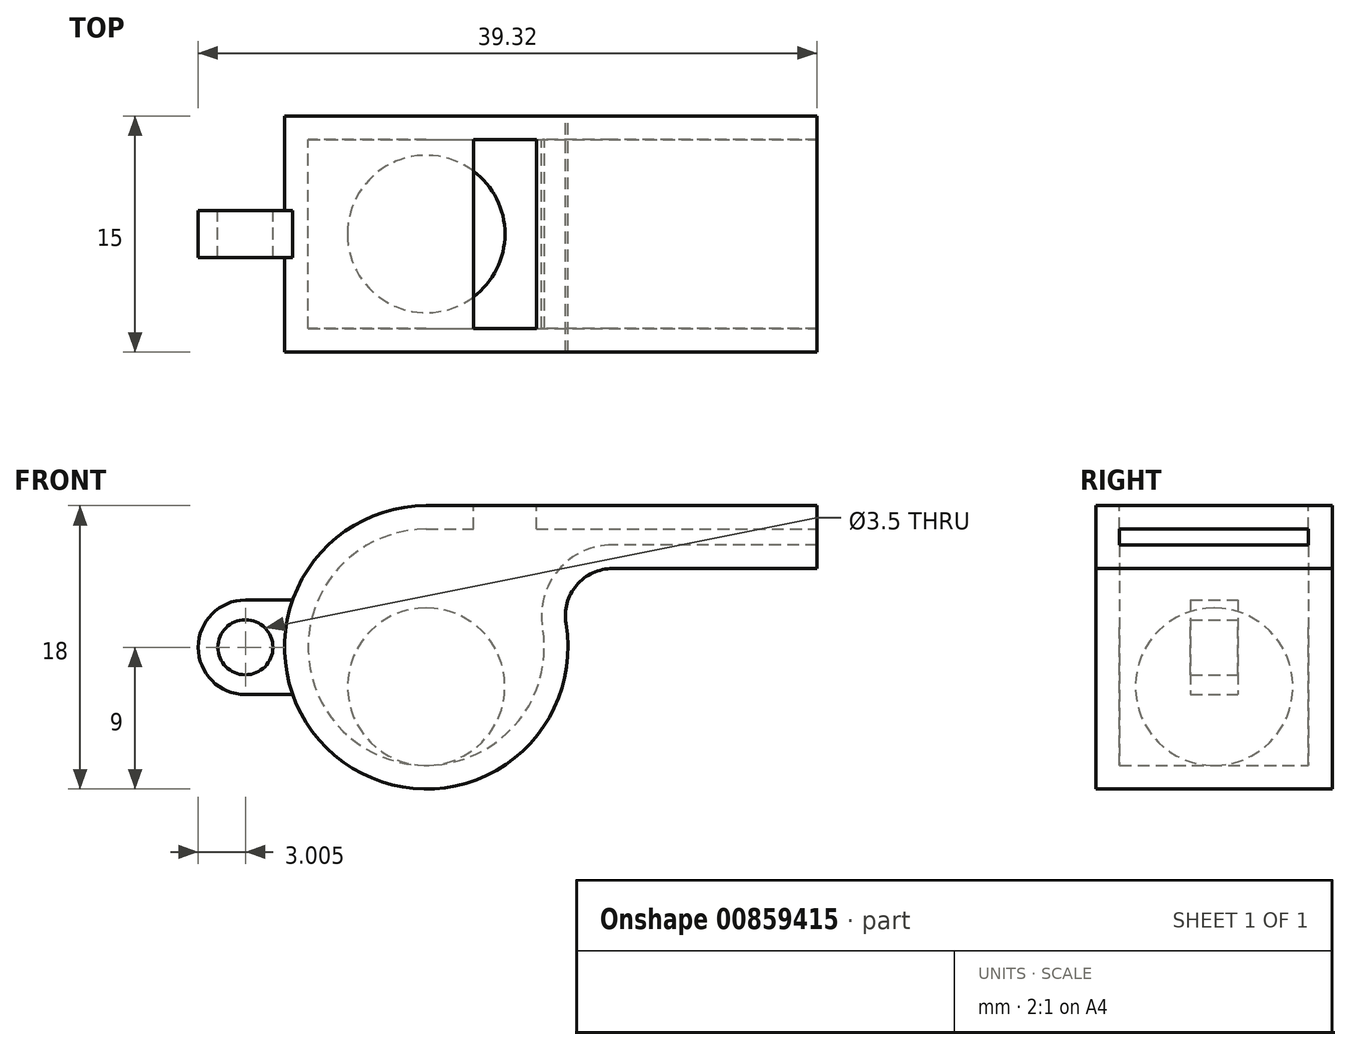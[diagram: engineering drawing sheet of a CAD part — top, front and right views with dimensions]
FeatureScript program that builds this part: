
annotation { "Feature Type Name" : "Feature", "Feature Type Description" : "" }
export const myFeature = defineFeature(function(context is Context, id is Id, definition is map)
    precondition{}
    {
        {
            var Q0;
            Q0=qCreatedBy(makeId("Front.planeOp"),FACE);
            var sketch = newSketch(context, id + "F0", { "sketchPlane" : qUnion([Q0])});
            skArc(sketch, "E0", {"start": v(0, 9) * mm, "mid": v(-5.8, -6.87) * mm, "end": v(8.87, 1.5) * mm});
            skLineSegment(sketch, "E1", {"start": v(0, 9) * mm, "end": v(24.83, 9) * mm});
            skLineSegment(sketch, "E2", {"start": v(24.83, 5) * mm, "end": v(11.83, 5) * mm});
            skArc(sketch, "E3.filletArc", {"start": v(11.83, 5) * mm, "mid": v(9.54, 3.94) * mm, "end": v(8.87, 1.5) * mm});
            skLineSegment(sketch, "E4", {"start": v(24.83, 9) * mm, "end": v(24.83, 5) * mm});
            skSolve(sketch);
        }
        {
            var Q0;
            Q0=makeQuery(id+"F0.imprint","IMPRINT",FACE,{"disambiguationData":[TD([[makeQuery(id+"F0.imprint","IMPRINT",EDGE,{"derivedFrom":sQuery(id+"F0.wireOp",EDGE,"E0")}),1.0]])]});
            extrude(context, id + "F1", {"entities" : qUnion([Q0]), "endBound" : BoundingType.SYMMETRIC, "depth" : 15 * mm, "offsetDistance" : 25 * mm});
        }
        {
            var Q0;
            Q0=makeQuery(id+"F1.opExtrude","SWEPT_FACE",FACE,{"disambiguationData":[OSD([sQuery(id+"F0.wireOp",EDGE,"E4")])]});
            shell(context, id + "F2", {"entities" : qUnion([Q0]), "thickness" : 1.5 * mm});
        }
        {
            var Q0;
            Q0=makeQuery(id+"F1.opExtrude","SWEPT_FACE",FACE,{"disambiguationData":[OSD([sQuery(id+"F0.wireOp",EDGE,"E1")])]});
            var sketch = newSketch(context, id + "F3", { "sketchPlane" : qUnion([Q0])});
            skLineSegment(sketch, "E5.bottom", {"start": v(3, 6) * mm, "end": v(7, 6) * mm});
            skLineSegment(sketch, "E5.top", {"start": v(3, -6) * mm, "end": v(7, -6) * mm});
            skLineSegment(sketch, "E5.left", {"start": v(3, 6) * mm, "end": v(3, -6) * mm});
            skLineSegment(sketch, "E5.right", {"start": v(7, 6) * mm, "end": v(7, -6) * mm});
            skSolve(sketch);
        }
        {
            var Q0;
            Q0 = qSketchRegion(id + "F3", true);
            extrude(context, id + "F4", {"entities" : qUnion([Q0]), "operationType" : NewBodyOperationType.REMOVE, "oppositeDirection" : true, "depth" : 1.5 * mm, "offsetDistance" : 25 * mm});
        }
        {
            var Q0;
            Q0=qCreatedBy(makeId("Front.planeOp"),FACE);
            var sketch = newSketch(context, id + "F5", { "sketchPlane" : qUnion([Q0])});
            skLineSegment(sketch, "E6.bottom", {"start": v(-11.49, 3) * mm, "end": v(-8.49, 3) * mm});
            skLineSegment(sketch, "E6.top", {"start": v(-11.49, -3) * mm, "end": v(-8.49, -3) * mm});
            skLineSegment(sketch, "E6.right", {"start": v(-8.49, 3) * mm, "end": v(-8.49, -3) * mm});
            skArc(sketch, "E7", {"start": v(-11.49, 3) * mm, "mid": v(-14.49, 0) * mm, "end": v(-11.49, -3) * mm});
            skCircle(sketch, "E8", {"center": v(-11.49, 0) * mm, "radius": 1.75 * mm});
            skSolve(sketch);
        }
        {
            var Q0;
            Q0 = qSketchRegion(id + "F5", true);
            extrude(context, id + "F6", {"entities" : qUnion([Q0]), "operationType" : NewBodyOperationType.ADD, "endBound" : BoundingType.SYMMETRIC, "depth" : 3 * mm, "offsetDistance" : 25 * mm});
        }
        {
            var Q0;
            Q0=qCreatedBy(makeId("Front.planeOp"),FACE);
            var sketch = newSketch(context, id + "F7", { "sketchPlane" : qUnion([Q0])});
            skArc(sketch, "E9", {"start": v(0, -7.5) * mm, "mid": v(5, -2.5) * mm, "end": v(0, 2.5) * mm});
            skLineSegment(sketch, "E10", {"start": v(0, 2.5) * mm, "end": v(0, -7.5) * mm});
            skSolve(sketch);
        }
        {
            var Q0;
            Q0 = qSketchRegion(id + "F7", true);
            var Q1;
            Q1=sQuery(id+"F7.wireOp",EDGE,"E9");
            var Q2;
            Q2=sQuery(id+"F7.wireOp",EDGE,"E10");
            var Q3;
            Q3=sQuery(id+"F7.wireOp",EDGE,"E10");
            revolve(context, id + "F8", {"surfaceOperationType" : NewSurfaceOperationType.NEW, "entities" : qUnion([Q0]), "surfaceEntities" : qUnion([Q1, Q2]), "axis" : qUnion([Q3]), "revolveType" : RevolveType.FULL});
        }
    });
